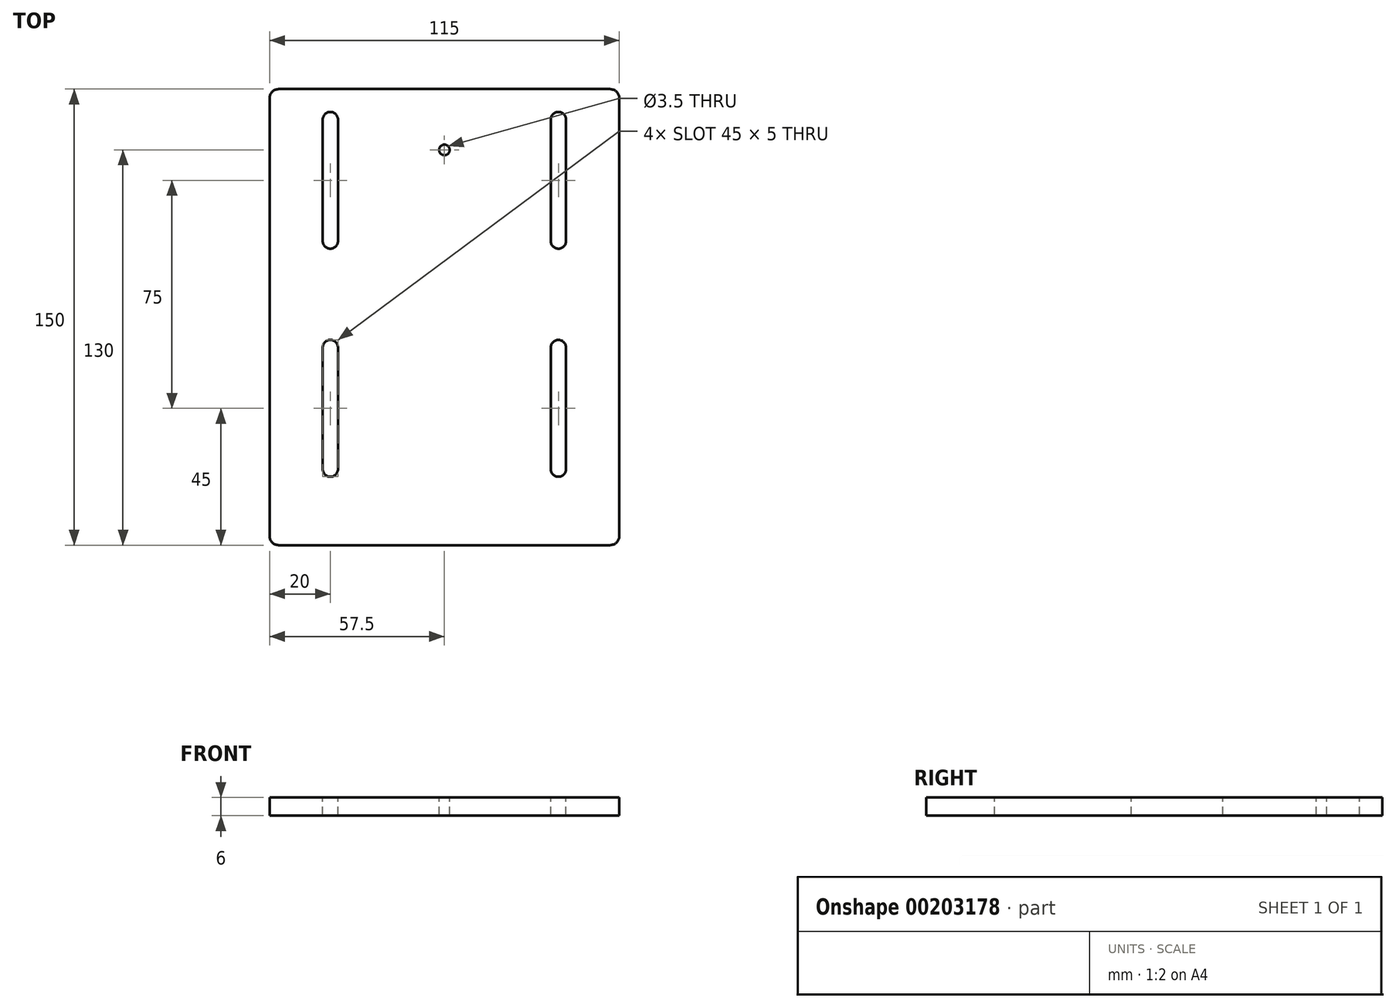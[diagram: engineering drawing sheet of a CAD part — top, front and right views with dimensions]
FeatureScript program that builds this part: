
annotation { "Feature Type Name" : "Feature", "Feature Type Description" : "" }
export const myFeature = defineFeature(function(context is Context, id is Id, definition is map)
    precondition{}
    {
        {
            var Q0;
            Q0=qCreatedBy(makeId("Top.planeOp"),FACE);
            var sketch = newSketch(context, id + "F0", { "sketchPlane" : qUnion([Q0])});
            skLineSegment(sketch, "E0.bottom", {"start": v(54.5, -75) * mm, "end": v(-54.5, -75) * mm});
            skLineSegment(sketch, "E0.top", {"start": v(54.5, 75) * mm, "end": v(-54.5, 75) * mm});
            skLineSegment(sketch, "E0.left", {"start": v(57.5, -72) * mm, "end": v(57.5, 72) * mm});
            skLineSegment(sketch, "E0.right", {"start": v(-57.5, -72) * mm, "end": v(-57.5, 72) * mm});
            skPoint(sketch, "E0.middle", {"position": v(0, 0) * mm});
            skPoint(sketch, "E1.visualSharp", {"position": v(-57.5, 75) * mm});
            skArc(sketch, "E1.filletArc", {"start": v(-54.5, 75) * mm, "mid": v(-56.62, 74.12) * mm, "end": v(-57.5, 72) * mm});
            skPoint(sketch, "E2.visualSharp", {"position": v(57.5, 75) * mm});
            skArc(sketch, "E2.filletArc", {"start": v(57.5, 72) * mm, "mid": v(56.62, 74.12) * mm, "end": v(54.5, 75) * mm});
            skPoint(sketch, "E3.visualSharp", {"position": v(-57.5, -75) * mm});
            skArc(sketch, "E3.filletArc", {"start": v(-57.5, -72) * mm, "mid": v(-56.62, -74.12) * mm, "end": v(-54.5, -75) * mm});
            skPoint(sketch, "E4.visualSharp", {"position": v(57.5, -75) * mm});
            skArc(sketch, "E4.filletArc", {"start": v(54.5, -75) * mm, "mid": v(56.62, -74.12) * mm, "end": v(57.5, -72) * mm});
            skSolve(sketch);
        }
        {
            var Q0;
            Q0=makeQuery(id+"F0.imprint","IMPRINT",FACE,{"disambiguationData":[TD([[makeQuery(id+"F0.imprint","IMPRINT",EDGE,{"derivedFrom":sQuery(id+"F0.wireOp",EDGE,"E0.bottom")}),-1.0]])]});
            extrude(context, id + "F1", {"entities" : qUnion([Q0]), "depth" : 6 * mm});
        }
        {
            var Q0;
            Q0=makeQuery(id+"F1.opExtrude","CAP_FACE",FACE,{"disambiguationData":[OSD([sQuery(id+"F0.wireOp",EDGE,"E0.bottom"),sQuery(id+"F0.wireOp",EDGE,"E0.top"),sQuery(id+"F0.wireOp",EDGE,"E0.left"),sQuery(id+"F0.wireOp",EDGE,"E0.right"),sQuery(id+"F0.wireOp",EDGE,"E1.filletArc"),sQuery(id+"F0.wireOp",EDGE,"E2.filletArc"),sQuery(id+"F0.wireOp",EDGE,"E3.filletArc"),sQuery(id+"F0.wireOp",EDGE,"E4.filletArc")])],"isStart":false});
            var sketch = newSketch(context, id + "F2", { "sketchPlane" : qUnion([Q0])});
            skLineSegment(sketch, "E5", {"start": v(-37.5, 65) * mm, "end": v(-37.5, 25) * mm});
            skLineSegment(sketch, "E6", {"start": v(37.5, 65) * mm, "end": v(37.5, 25) * mm});
            skLineSegment(sketch, "E7", {"start": v(37.5, -10) * mm, "end": v(37.5, -50) * mm});
            skLineSegment(sketch, "E8", {"start": v(-37.5, -10) * mm, "end": v(-37.5, -50) * mm});
            skLineSegment(sketch, "E9", {"start": v(-37.5, 65) * mm, "end": v(37.5, 65) * mm, "construction": true});
            skLineSegment(sketch, "E10", {"start": v(37.5, -50) * mm, "end": v(-37.5, -50) * mm, "construction": true});
            skLineSegment(sketch, "E11", {"start": v(0, 65) * mm, "end": v(0, -50) * mm});
            skArc(sketch, "E12.0.startCap", {"start": v(-40, 65) * mm, "mid": v(-37.5, 67.5) * mm, "end": v(-35, 65) * mm});
            skArc(sketch, "E12.0.endCap", {"start": v(-35, 25) * mm, "mid": v(-37.5, 22.5) * mm, "end": v(-40, 25) * mm});
            skLineSegment(sketch, "E12.0.left", {"start": v(-35, 65) * mm, "end": v(-35, 25) * mm});
            skLineSegment(sketch, "E12.0.right", {"start": v(-40, 65) * mm, "end": v(-40, 25) * mm});
            skArc(sketch, "E12.1.startCap", {"start": v(35, 65) * mm, "mid": v(37.5, 67.5) * mm, "end": v(40, 65) * mm});
            skArc(sketch, "E12.1.endCap", {"start": v(40, 25) * mm, "mid": v(37.5, 22.5) * mm, "end": v(35, 25) * mm});
            skLineSegment(sketch, "E12.1.left", {"start": v(40, 65) * mm, "end": v(40, 25) * mm});
            skLineSegment(sketch, "E12.1.right", {"start": v(35, 65) * mm, "end": v(35, 25) * mm});
            skArc(sketch, "E12.2.startCap", {"start": v(35, -10) * mm, "mid": v(37.5, -7.5) * mm, "end": v(40, -10) * mm});
            skArc(sketch, "E12.2.endCap", {"start": v(40, -50) * mm, "mid": v(37.5, -52.5) * mm, "end": v(35, -50) * mm});
            skLineSegment(sketch, "E12.2.left", {"start": v(40, -10) * mm, "end": v(40, -50) * mm});
            skLineSegment(sketch, "E12.2.right", {"start": v(35, -10) * mm, "end": v(35, -50) * mm});
            skArc(sketch, "E12.3.startCap", {"start": v(-40, -10) * mm, "mid": v(-37.5, -7.5) * mm, "end": v(-35, -10) * mm});
            skArc(sketch, "E12.3.endCap", {"start": v(-35, -50) * mm, "mid": v(-37.5, -52.5) * mm, "end": v(-40, -50) * mm});
            skLineSegment(sketch, "E12.3.left", {"start": v(-35, -10) * mm, "end": v(-35, -50) * mm});
            skLineSegment(sketch, "E12.3.right", {"start": v(-40, -10) * mm, "end": v(-40, -50) * mm});
            skSolve(sketch);
        }
        {
            var Q0;
            Q0 = qSketchRegion(id + "F2", true);
            extrude(context, id + "F3", {"entities" : qUnion([Q0]), "operationType" : NewBodyOperationType.REMOVE, "endBound" : BoundingType.UP_TO_NEXT, "oppositeDirection" : true, "depth" : 25 * mm});
        }
        {
            var Q0;
            Q0=makeQuery(id+"F1.opExtrude","CAP_FACE",FACE,{"disambiguationData":[OSD([sQuery(id+"F0.wireOp",EDGE,"E0.bottom"),sQuery(id+"F0.wireOp",EDGE,"E0.top"),sQuery(id+"F0.wireOp",EDGE,"E0.left"),sQuery(id+"F0.wireOp",EDGE,"E0.right"),sQuery(id+"F0.wireOp",EDGE,"E1.filletArc"),sQuery(id+"F0.wireOp",EDGE,"E2.filletArc"),sQuery(id+"F0.wireOp",EDGE,"E3.filletArc"),sQuery(id+"F0.wireOp",EDGE,"E4.filletArc")])],"isStart":false});
            var sketch = newSketch(context, id + "F4", { "sketchPlane" : qUnion([Q0])});
            skCircle(sketch, "E13", {"center": v(0, 55) * mm, "radius": 1.75 * mm});
            skSolve(sketch);
        }
        {
            var Q0;
            Q0 = qSketchRegion(id + "F4", true);
            extrude(context, id + "F5", {"entities" : qUnion([Q0]), "operationType" : NewBodyOperationType.REMOVE, "endBound" : BoundingType.UP_TO_NEXT, "oppositeDirection" : true, "depth" : 25 * mm});
        }
    });
